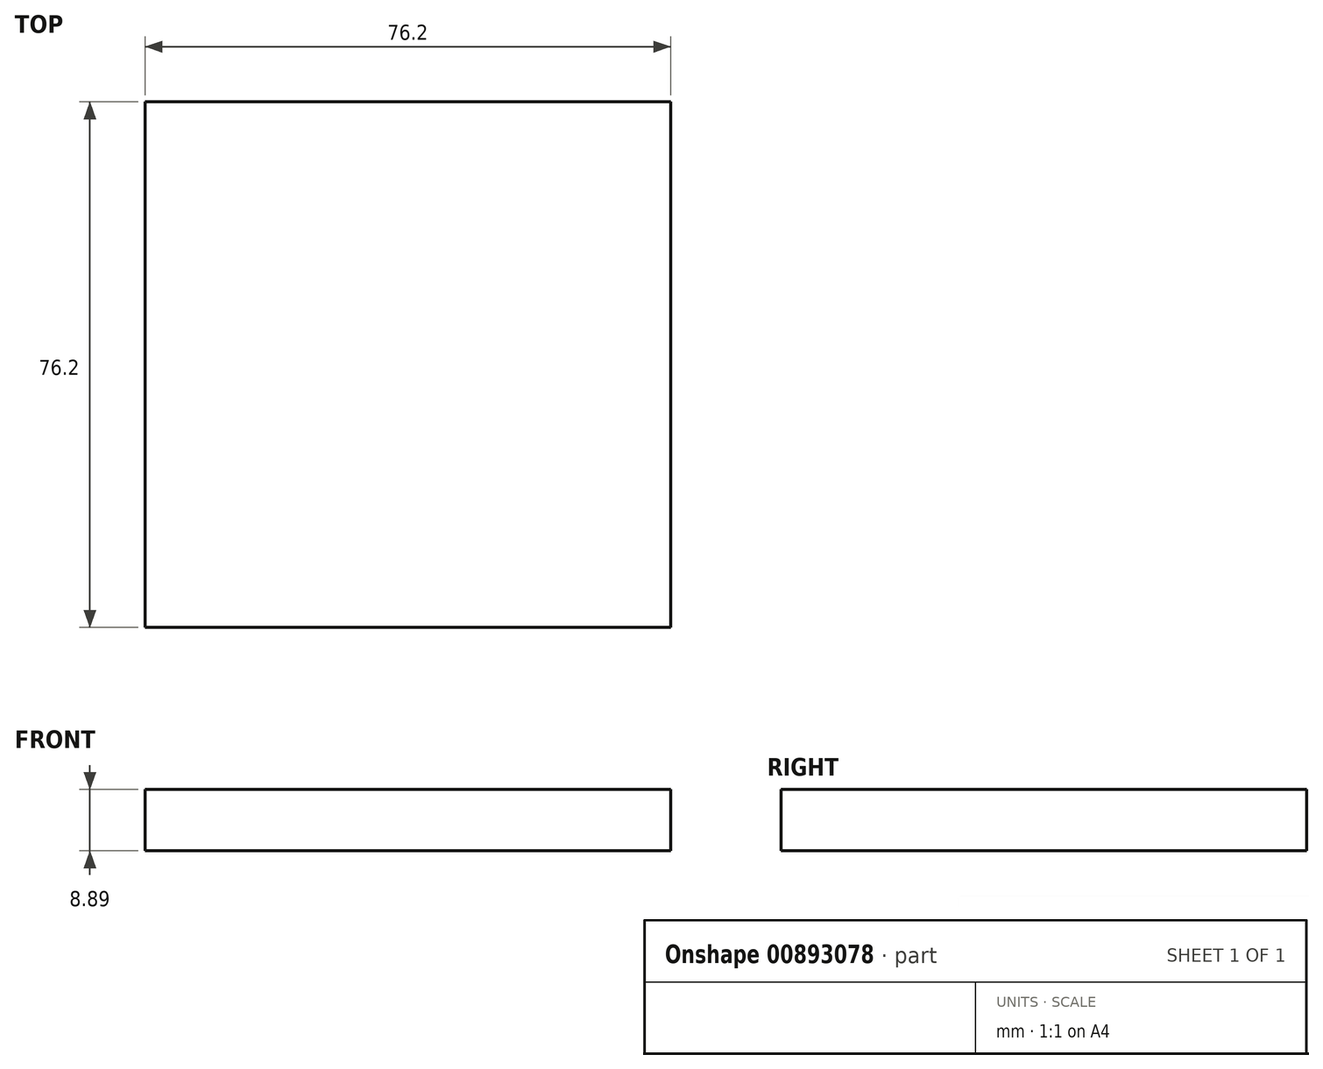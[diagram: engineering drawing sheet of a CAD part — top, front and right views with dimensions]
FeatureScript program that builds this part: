
annotation { "Feature Type Name" : "Feature", "Feature Type Description" : "" }
export const myFeature = defineFeature(function(context is Context, id is Id, definition is map)
    precondition{}
    {
        {
            var Q0;
            Q0=qCreatedBy(makeId("Top.planeOp"),FACE);
            var sketch = newSketch(context, id + "F0", { "sketchPlane" : qUnion([Q0])});
            skLineSegment(sketch, "E0.bottom", {"start": v(-37.25, 26.87) * mm, "end": v(38.95, 26.87) * mm});
            skLineSegment(sketch, "E0.top", {"start": v(-37.25, -49.33) * mm, "end": v(38.95, -49.33) * mm});
            skLineSegment(sketch, "E0.left", {"start": v(-37.25, 26.87) * mm, "end": v(-37.25, -49.33) * mm});
            skLineSegment(sketch, "E0.right", {"start": v(38.95, 26.87) * mm, "end": v(38.95, -49.33) * mm});
            skSolve(sketch);
        }
        {
            var Q0;
            Q0 = qSketchRegion(id + "F0", true);
            extrude(context, id + "F1", {"entities" : qUnion([Q0]), "depth" : 8.9 * mm, "offsetDistance" : 25.4 * mm});
        }
    });
